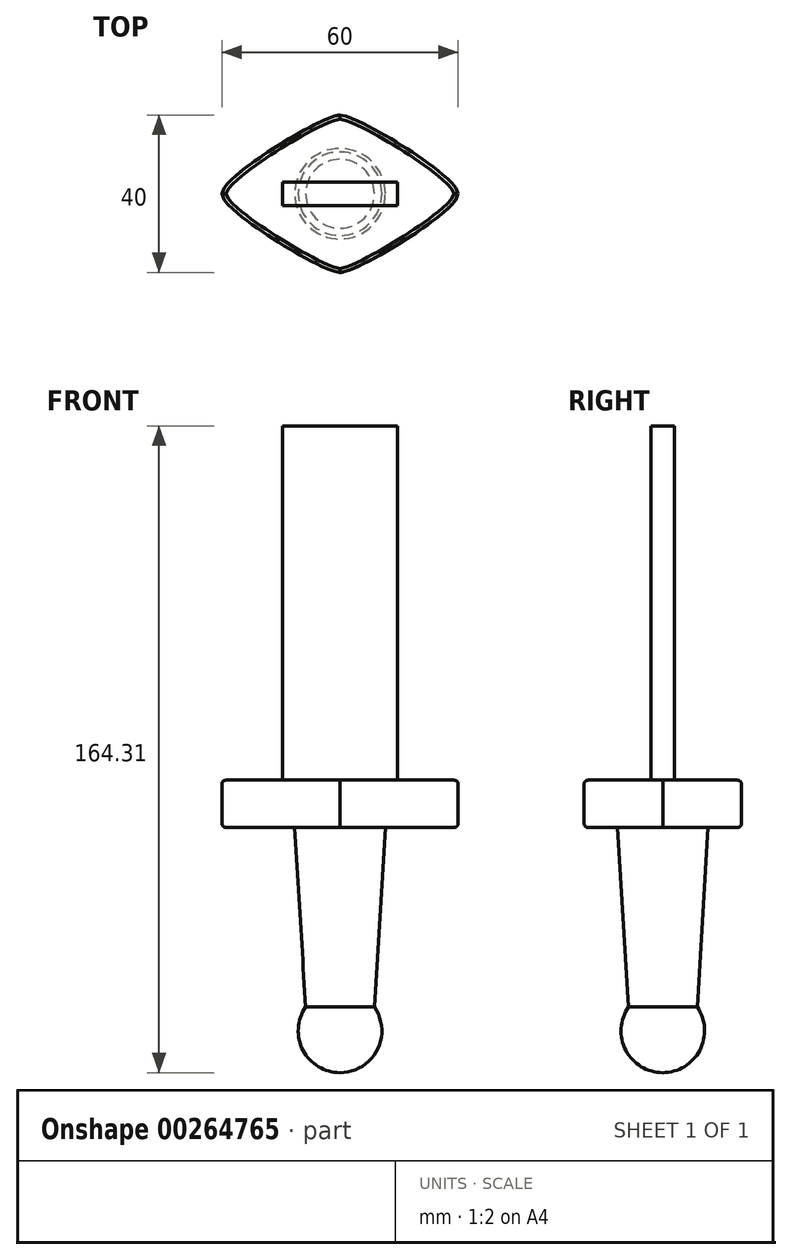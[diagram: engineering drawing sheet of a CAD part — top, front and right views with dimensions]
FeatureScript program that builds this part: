
annotation { "Feature Type Name" : "Feature", "Feature Type Description" : "" }
export const myFeature = defineFeature(function(context is Context, id is Id, definition is map)
    precondition{}
    {
        {
            var Q0;
            Q0=qCreatedBy(makeId("Top.planeOp"),FACE);
            var sketch = newSketch(context, id + "F0", { "sketchPlane" : qUnion([Q0])});
            skLineSegment(sketch, "E0", {"start": v(0, 0) * mm, "end": v(0, 20) * mm, "construction": true});
            skLineSegment(sketch, "E1", {"start": v(0, 0) * mm, "end": v(-30, 0) * mm, "construction": true});
            skLineSegment(sketch, "E2", {"start": v(0, 20) * mm, "end": v(-30, 0) * mm, "construction": true});
            skFitSpline(sketch, "E3", {"points": [v(0, 20) * mm, v(-30, 0) * mm], "startDerivative": vector(-13.68, -0.36) * mm, "endDerivative": vector(0.1, -13.3) * mm});
            skFitSpline(sketch, "E4.MirrorCS", {"points": [v(0, 20) * mm, v(30, 0) * mm], "startDerivative": vector(13.68, -0.36) * mm, "endDerivative": vector(-0.1, -13.3) * mm});
            skFitSpline(sketch, "E5.MirrorCS", {"points": [v(0, -20) * mm, v(-30, 0) * mm], "startDerivative": vector(-13.68, 0.36) * mm, "endDerivative": vector(0.1, 13.3) * mm});
            skFitSpline(sketch, "E6.MirrorCS", {"points": [v(0, -20) * mm, v(30, 0) * mm], "startDerivative": vector(13.68, 0.36) * mm, "endDerivative": vector(-0.1, 13.3) * mm});
            skSolve(sketch);
        }
        {
            var Q0;
            Q0=makeQuery(id+"F0.imprint","IMPRINT",FACE,{"disambiguationData":[TD([[makeQuery(id+"F0.imprint","IMPRINT",EDGE,{"derivedFrom":sQuery(id+"F0.wireOp",EDGE,"E3")}),1.0]])]});
            extrude(context, id + "F1", {"entities" : qUnion([Q0]), "depth" : 12 * mm, "offsetDistance" : 25 * mm});
        }
        {
            var Q0;
            Q0=makeQuery(id+"F1.opExtrude","CAP_FACE",FACE,{"disambiguationData":[OSD([sQuery(id+"F0.wireOp",EDGE,"E3"),sQuery(id+"F0.wireOp",EDGE,"E4.MirrorCS"),sQuery(id+"F0.wireOp",EDGE,"E5.MirrorCS"),sQuery(id+"F0.wireOp",EDGE,"E6.MirrorCS")])],"isStart":false});
            var Q1;
            Q1=makeQuery(id+"F1.opExtrude","CAP_FACE",FACE,{"disambiguationData":[OSD([sQuery(id+"F0.wireOp",EDGE,"E3"),sQuery(id+"F0.wireOp",EDGE,"E4.MirrorCS"),sQuery(id+"F0.wireOp",EDGE,"E5.MirrorCS"),sQuery(id+"F0.wireOp",EDGE,"E6.MirrorCS")])],"isStart":true});
            fillet(context, id + "F2", {"entities" : qUnion([Q0, Q1]), "radius" : 1 * mm, "tangentPropagation" : true, "allowEdgeOverflow" : false});
        }
        {
            var Q0;
            Q0=makeQuery(id+"F1.opExtrude","CAP_FACE",FACE,{"disambiguationData":[OSD([sQuery(id+"F0.wireOp",EDGE,"E3"),sQuery(id+"F0.wireOp",EDGE,"E4.MirrorCS"),sQuery(id+"F0.wireOp",EDGE,"E5.MirrorCS"),sQuery(id+"F0.wireOp",EDGE,"E6.MirrorCS")])],"isStart":true});
            var sketch = newSketch(context, id + "F3", { "sketchPlane" : qUnion([Q0])});
            skCircle(sketch, "E7", {"center": v(0, 0) * mm, "radius": 11.5 * mm});
            skLineSegment(sketch, "E8", {"start": v(-11.5, 0) * mm, "end": v(11.5, 0) * mm, "construction": true});
            skSolve(sketch);
        }
        {
            var Q0;
            Q0=qCreatedBy(makeId("Top.planeOp"),FACE);
            cPlane(context, id + "F4", {"entities" : qUnion([Q0]), "cplaneType" : CPlaneType.OFFSET, "offset" : 50 * mm, "oppositeDirection" : true, "width" : 150 * mm, "height" : 150 * mm});
        }
        {
            var Q0;
            Q0=qCreatedBy(id+"F4.planeOp",FACE);
            var sketch = newSketch(context, id + "F5", { "sketchPlane" : qUnion([Q0])});
            skCircle(sketch, "E9", {"center": v(0, 0) * mm, "radius": 8.48 * mm});
            skSolve(sketch);
        }
        {
            var Q1;
            Q1=makeQuery(id+"F3.imprint","IMPRINT",FACE,{"disambiguationData":[TD([[makeQuery(id+"F3.imprint","IMPRINT",EDGE,{"derivedFrom":sQuery(id+"F3.wireOp",EDGE,"E7")}),1.0]])]});
            var Q2;
            Q2=makeQuery(id+"F5.imprint","IMPRINT",FACE,{"disambiguationData":[TD([[makeQuery(id+"F5.imprint","IMPRINT",EDGE,{"derivedFrom":sQuery(id+"F5.wireOp",EDGE,"E9")}),1.0]])]});
            loft(context, id + "F6", {"operationType" : NewBodyOperationType.ADD, "sheetProfilesArray" : [{ "sheetProfileEntities" : qUnion([Q1]) }, { "sheetProfileEntities" : qUnion([Q2]) }]});
        }
        {
            var Q0;
            Q0=qCreatedBy(makeId("Front.planeOp"),FACE);
            var sketch = newSketch(context, id + "F7", { "sketchPlane" : qUnion([Q0])});
            skCircle(sketch, "E10", {"center": v(0, -51.69) * mm, "radius": 10.62 * mm});
            skLineSegment(sketch, "E11", {"start": v(0, -41.07) * mm, "end": v(0, -62.3) * mm});
            skSolve(sketch);
        }
        {
            var Q0;
            {var subQ0=sQuery(id+"F7.wireOp",EDGE,"E11");Q0=makeQuery(id+"F7.imprint","IMPRINT",FACE,{"disambiguationData":[TD([[makeQuery(id+"F7.imprint","IMPRINT",EDGE,{"derivedFrom":subQ0}),-1.0]])]});}
            var Q1;
            Q1=sQuery(id+"F7.wireOp",EDGE,"E11");
            revolve(context, id + "F8", {"operationType" : NewBodyOperationType.ADD, "surfaceOperationType" : NewSurfaceOperationType.NEW, "entities" : qUnion([Q0]), "axis" : qUnion([Q1]), "revolveType" : RevolveType.FULL});
        }
        {
            var Q0;
            Q0=makeQuery(id+"F1.opExtrude","CAP_FACE",FACE,{"disambiguationData":[OSD([sQuery(id+"F0.wireOp",EDGE,"E3"),sQuery(id+"F0.wireOp",EDGE,"E4.MirrorCS"),sQuery(id+"F0.wireOp",EDGE,"E5.MirrorCS"),sQuery(id+"F0.wireOp",EDGE,"E6.MirrorCS")])],"isStart":false});
            var sketch = newSketch(context, id + "F9", { "sketchPlane" : qUnion([Q0])});
            skLineSegment(sketch, "E12", {"start": v(0, 0) * mm, "end": v(0, 3) * mm, "construction": true});
            skLineSegment(sketch, "E13", {"start": v(0, 3) * mm, "end": v(-14.58, 3) * mm, "construction": true});
            skLineSegment(sketch, "E14.MirrorCS", {"start": v(0, -3) * mm, "end": v(-14.58, -3) * mm, "construction": true});
            skLineSegment(sketch, "E15.MirrorCS", {"start": v(0, 3) * mm, "end": v(14.58, 3) * mm, "construction": true});
            skLineSegment(sketch, "E16.MirrorCS", {"start": v(0, -3) * mm, "end": v(14.58, -3) * mm, "construction": true});
            skLineSegment(sketch, "E17", {"start": v(-14.58, 3) * mm, "end": v(-14.58, -3) * mm});
            skLineSegment(sketch, "E18", {"start": v(14.58, 3) * mm, "end": v(14.58, -3) * mm});
            skLineSegment(sketch, "E19", {"start": v(14.58, -3) * mm, "end": v(-14.58, -3) * mm});
            skLineSegment(sketch, "E20", {"start": v(-14.58, 3) * mm, "end": v(14.58, 3) * mm});
            skSolve(sketch);
        }
        {
            var Q0;
            Q0=makeQuery(id+"F9.imprint","IMPRINT",FACE,{"disambiguationData":[TD([[makeQuery(id+"F9.imprint","IMPRINT",EDGE,{"derivedFrom":sQuery(id+"F9.wireOp",EDGE,"E17")}),1.0]])]});
            extrude(context, id + "F10", {"entities" : qUnion([Q0]), "operationType" : NewBodyOperationType.ADD, "depth" : 90 * mm, "offsetDistance" : 25 * mm});
        }
        {
            var Q0;
            Q0=qCreatedBy(makeId("Front.planeOp"),FACE);
            cPlane(context, id + "F11", {"entities" : qUnion([Q0]), "cplaneType" : CPlaneType.OFFSET, "offset" : 6 * mm, "width" : 150 * mm, "height" : 150 * mm});
        }
    });
